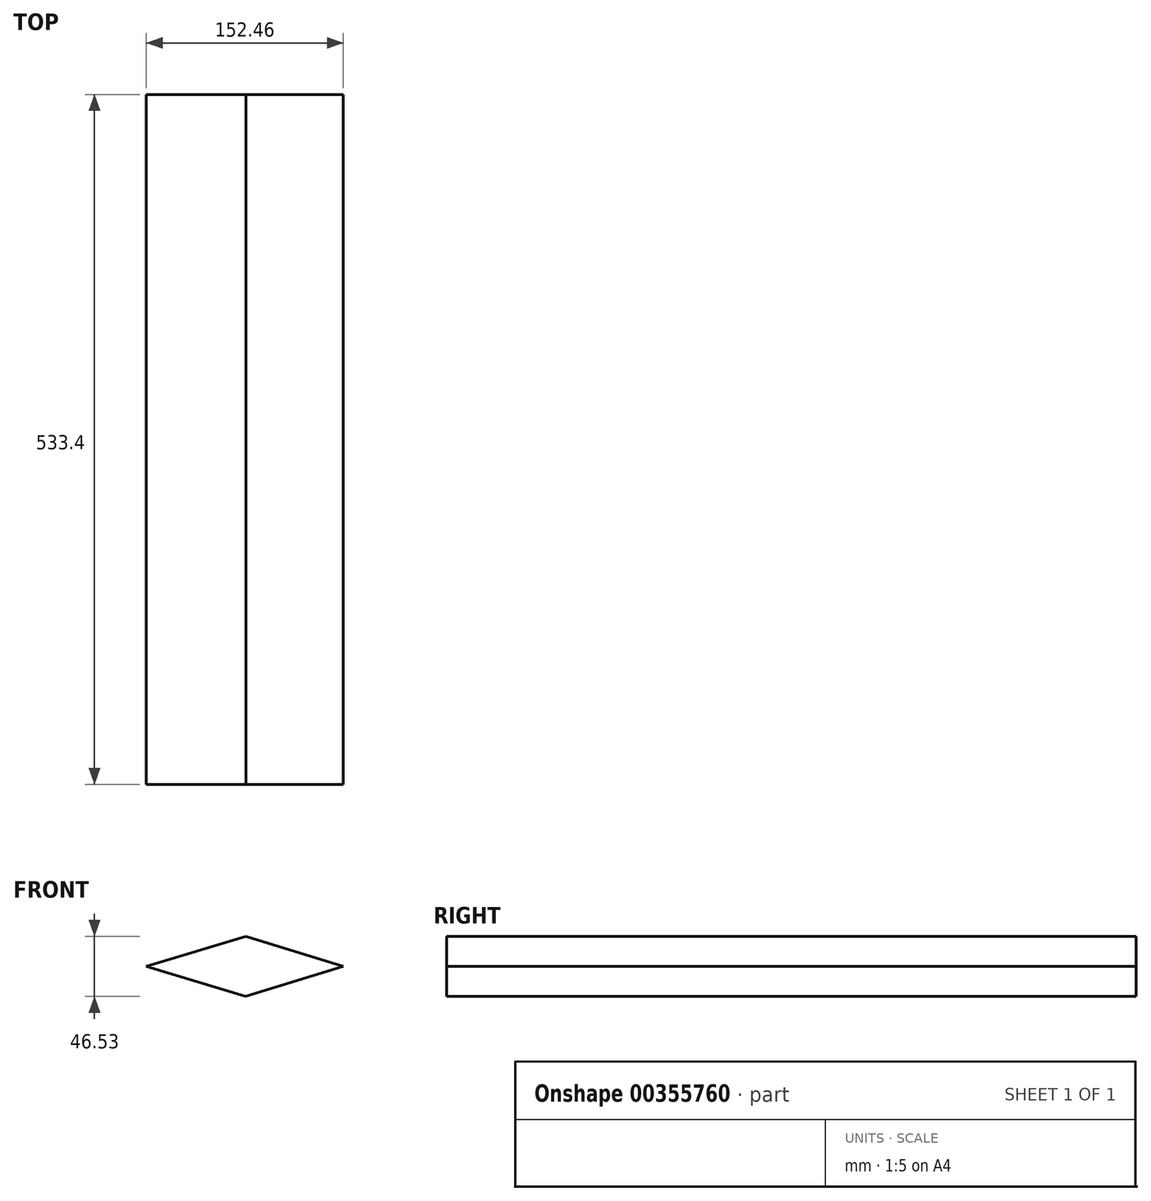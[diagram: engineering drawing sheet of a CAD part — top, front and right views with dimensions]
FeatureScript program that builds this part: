
annotation { "Feature Type Name" : "Feature", "Feature Type Description" : "" }
export const myFeature = defineFeature(function(context is Context, id is Id, definition is map)
    precondition{}
    {
        {
            var Q0;
            Q0=qCreatedBy(makeId("Front.planeOp"),FACE);
            var sketch = newSketch(context, id + "F0", { "sketchPlane" : qUnion([Q0])});
            skCircle(sketch, "E0", {"center": v(0, 0) * mm, "radius": 23.27 * mm});
            skLineSegment(sketch, "E1", {"start": v(-76.68, 0) * mm, "end": v(75.78, 0) * mm});
            skLineSegment(sketch, "E2", {"start": v(75.78, 0) * mm, "end": v(0.43, 23.26) * mm});
            skLineSegment(sketch, "E3", {"start": v(0.43, 23.26) * mm, "end": v(-76.68, 0) * mm});
            skLineSegment(sketch, "E4", {"start": v(0, -23.27) * mm, "end": v(-76.68, 0) * mm});
            skLineSegment(sketch, "E5", {"start": v(75.78, 0) * mm, "end": v(0, -23.27) * mm});
            skSolve(sketch);
        }
        {
            var Q0;
            {var subQ1=sQuery(id+"F0.wireOp",EDGE,"E4");var subQ2=sQuery(id+"F0.wireOp",EDGE,"E0");var subQ4=makeQuery(id+"F0.imprint","INTERSECT",VERTEX,{"derivedFrom":[subQ2,subQ1]});Q0=makeQuery(id+"F0.imprint","IMPRINT",FACE,{"disambiguationData":[TD([[makeQuery(id+"F0.imprint","IMPRINT",EDGE,{"disambiguationData":[TD([[subQ4,1.0]])],"derivedFrom":subQ2}),1.0]])]});}
            var Q1;
            {var subQ1=sQuery(id+"F0.wireOp",EDGE,"E2");var subQ2=sQuery(id+"F0.wireOp",EDGE,"E0");var subQ4=makeQuery(id+"F0.imprint","INTERSECT",VERTEX,{"derivedFrom":[subQ2,subQ1]});Q1=makeQuery(id+"F0.imprint","IMPRINT",FACE,{"disambiguationData":[TD([[makeQuery(id+"F0.imprint","IMPRINT",EDGE,{"disambiguationData":[TD([[subQ4,1.0]])],"derivedFrom":subQ2}),1.0]])]});}
            var Q2;
            {var subQ0=sQuery(id+"F0.wireOp",EDGE,"E3");var subQ1=sQuery(id+"F0.wireOp",EDGE,"E0");var subQ2=makeQuery(id+"F0.imprint","INTERSECT",VERTEX,{"derivedFrom":[subQ1,subQ0]});Q2=makeQuery(id+"F0.imprint","IMPRINT",FACE,{"disambiguationData":[TD([[makeQuery(id+"F0.imprint","IMPRINT",EDGE,{"disambiguationData":[TD([[subQ2,-1.0]])],"derivedFrom":subQ1}),-1.0]])]});}
            var Q3;
            {var subQ0=sQuery(id+"F0.wireOp",EDGE,"E4");var subQ1=sQuery(id+"F0.wireOp",EDGE,"E0");var subQ2=makeQuery(id+"F0.imprint","INTERSECT",VERTEX,{"derivedFrom":[subQ1,subQ0]});Q3=makeQuery(id+"F0.imprint","IMPRINT",FACE,{"disambiguationData":[TD([[makeQuery(id+"F0.imprint","IMPRINT",EDGE,{"disambiguationData":[TD([[subQ2,1.0]])],"derivedFrom":subQ1}),-1.0]])]});}
            var Q4;
            {var subQ0=sQuery(id+"F0.wireOp",EDGE,"E2");var subQ1=sQuery(id+"F0.wireOp",EDGE,"E0");var subQ2=makeQuery(id+"F0.imprint","INTERSECT",VERTEX,{"derivedFrom":[subQ1,subQ0]});Q4=makeQuery(id+"F0.imprint","IMPRINT",FACE,{"disambiguationData":[TD([[makeQuery(id+"F0.imprint","IMPRINT",EDGE,{"disambiguationData":[TD([[subQ2,1.0]])],"derivedFrom":subQ1}),-1.0]])]});}
            var Q5;
            {var subQ0=sQuery(id+"F0.wireOp",EDGE,"E5");var subQ1=sQuery(id+"F0.wireOp",EDGE,"E0");var subQ2=makeQuery(id+"F0.imprint","INTERSECT",VERTEX,{"derivedFrom":[subQ1,subQ0]});Q5=makeQuery(id+"F0.imprint","IMPRINT",FACE,{"disambiguationData":[TD([[makeQuery(id+"F0.imprint","IMPRINT",EDGE,{"disambiguationData":[TD([[subQ2,-1.0]])],"derivedFrom":subQ1}),-1.0]])]});}
            extrude(context, id + "F1", {"entities" : qUnion([Q0, Q1, Q2, Q3, Q4, Q5]), "depth" : 25.4 * mm});
        }
        {
            var Q0;
            Q0=makeQuery(id+"F1.opExtrude","CAP_FACE",FACE,{"disambiguationData":[OSD([sQuery(id+"F0.wireOp",EDGE,"E2"),sQuery(id+"F0.wireOp",EDGE,"E3"),sQuery(id+"F0.wireOp",EDGE,"E4"),sQuery(id+"F0.wireOp",EDGE,"E5")])],"isStart":false});
            extrude(context, id + "F2", {"entities" : qUnion([Q0]), "operationType" : NewBodyOperationType.ADD, "depth" : 508 * mm});
        }
    });
